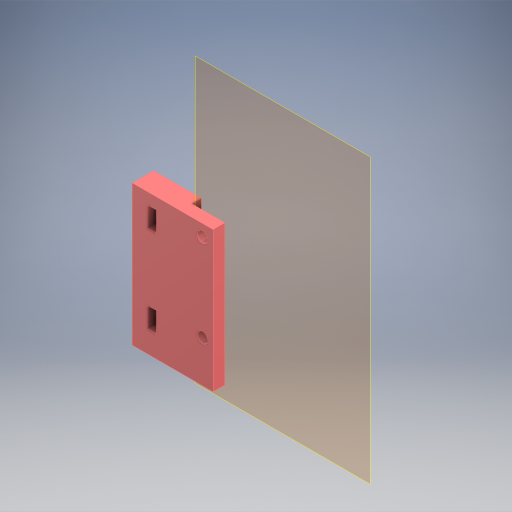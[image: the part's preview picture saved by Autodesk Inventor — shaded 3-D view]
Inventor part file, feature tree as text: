
AUTODESK INVENTOR PART (.ipt)
format: ipt  version: 2024 (Build 280153000, 153)  size: 385,536 bytes
history: native  units: in
note: dims shown in document units (in); Inventor stores cm internally (conversion verified against a paired STEP export)
features: other x6, reference x5, extrude x4, sketch x4, projected_geometry x1
ambient origin geometry x8: Origin, YZ Plane, XZ Plane, XY Plane, X Axis, Y Axis, Z Axis, Center Point
bodies: Body1 (feature_tree)
feature tree (20):
  other  "작업 평면1"
  extrude  "돌출8"  Depth=0.0039in
  extrude  "돌출10"  Depth=0.8031in
  extrude  "돌출11"  Depth=0.1181in TaperAngle=0.0deg
  extrude  "돌출12"  Depth=0.0039in
  sketch  "스케치2"
  reference  "참조2"
  reference  "참조3"
  sketch  "스케치10"
  reference  "참조8"
  projected_geometry  "투영된 루프5"
  sketch  "스케치12"
  reference  "참조9"
  reference  "참조10"
  sketch  "스케치13"
  other  "조립품1"
  other  "MX-106T+idle.ipt:1"
  other  "MX-106T:1"
  other  "MX-64T+idle.ipt:1"
  other  "MX-64T:1"
